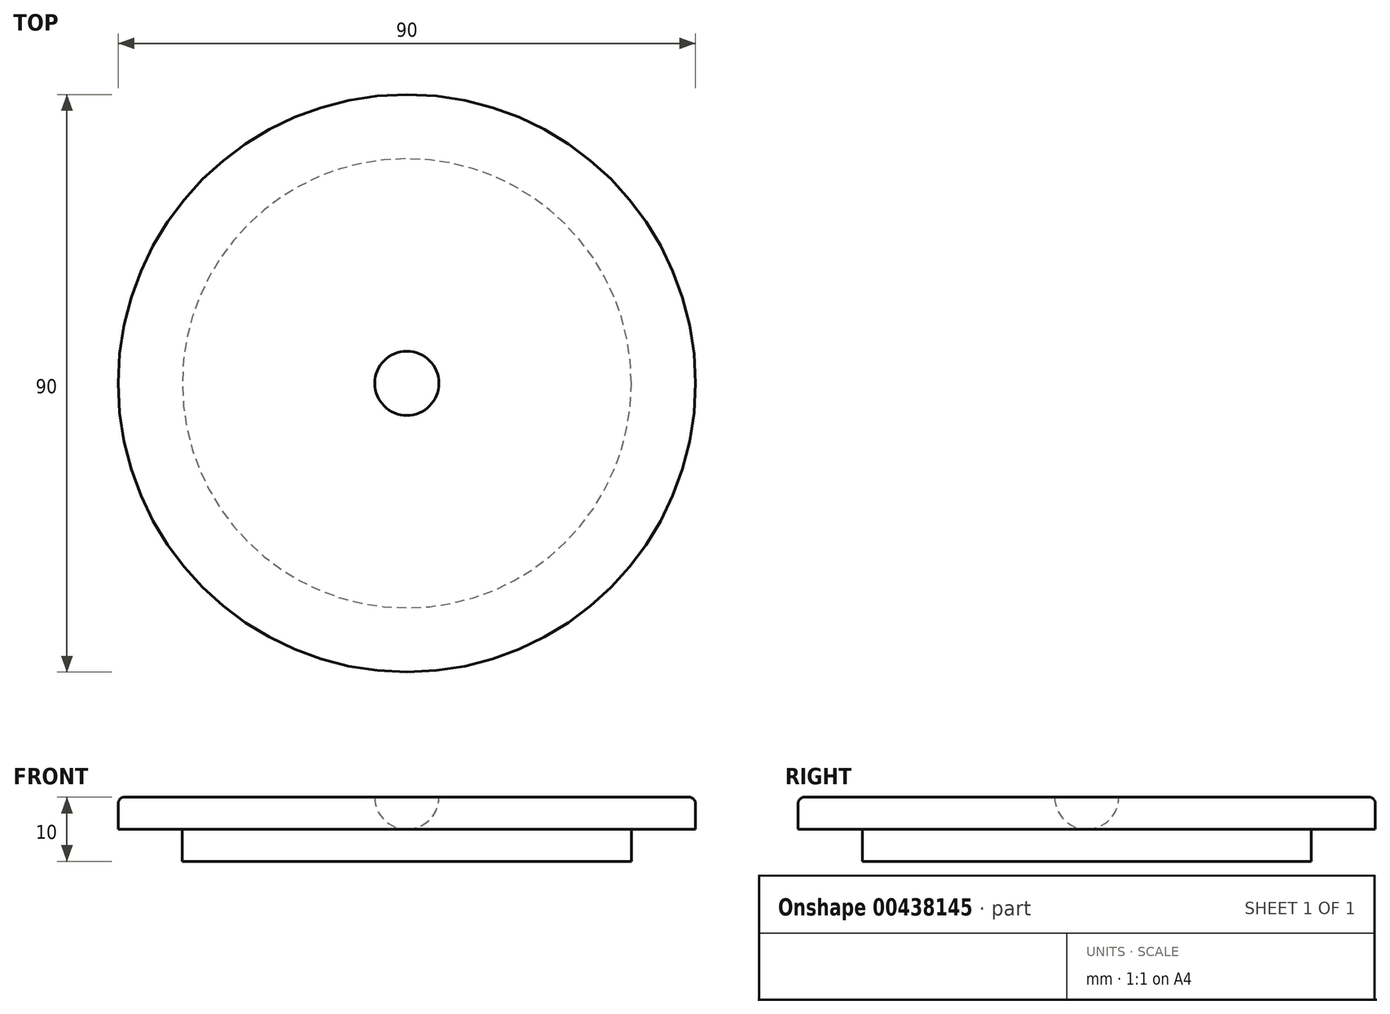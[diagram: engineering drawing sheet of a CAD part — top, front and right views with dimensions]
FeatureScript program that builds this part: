
annotation { "Feature Type Name" : "Feature", "Feature Type Description" : "" }
export const myFeature = defineFeature(function(context is Context, id is Id, definition is map)
    precondition{}
    {
        {
            var Q0;
            Q0=qCreatedBy(makeId("Front.planeOp"),FACE);
            var sketch = newSketch(context, id + "F0", { "sketchPlane" : qUnion([Q0])});
            skLineSegment(sketch, "E0", {"start": v(0, 0) * mm, "end": v(35, 0) * mm});
            skLineSegment(sketch, "E1", {"start": v(35, 0) * mm, "end": v(35, 5) * mm});
            skLineSegment(sketch, "E2", {"start": v(35, 5) * mm, "end": v(45, 5) * mm});
            skLineSegment(sketch, "E3", {"start": v(45, 5) * mm, "end": v(45, 10) * mm});
            skLineSegment(sketch, "E4", {"start": v(45, 10) * mm, "end": v(0, 10) * mm});
            skLineSegment(sketch, "E5", {"start": v(0, 10) * mm, "end": v(0, 0) * mm});
            skArc(sketch, "E6", {"start": v(0, 5) * mm, "mid": v(3.54, 6.46) * mm, "end": v(5, 10) * mm});
            skSolve(sketch);
        }
        {
            var Q0;
            {var subQ1=sQuery(id+"F0.wireOp",EDGE,"E0");Q0=makeQuery(id+"F0.imprint","IMPRINT",FACE,{"disambiguationData":[TD([[makeQuery(id+"F0.imprint","IMPRINT",EDGE,{"derivedFrom":subQ1}),1.0]])]});}
            var Q1;
            Q1=sQuery(id+"F0.wireOp",EDGE,"E5");
            revolve(context, id + "F1", {"entities" : qUnion([Q0]), "axis" : qUnion([Q1]), "revolveType" : RevolveType.FULL});
        }
        {
            var Q0;
            Q0=makeQuery(id+"F1.opRevolve","SWEPT_EDGE",EDGE,{"disambiguationData":[OSD([sQuery(id+"F0.wireOp",EDGE,"E3"),sQuery(id+"F0.wireOp",EDGE,"E4")])]});
            fillet(context, id + "F2", {"entities" : qUnion([Q0]), "radius" : 1 * mm, "tangentPropagation" : true, "allowEdgeOverflow" : false});
        }
    });
